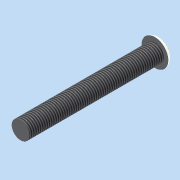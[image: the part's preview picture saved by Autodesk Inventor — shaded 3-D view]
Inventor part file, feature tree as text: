
AUTODESK INVENTOR PART (.ipt)
format: ipt  version: 2015 (Build 190159000, 159)  size: 96,256 bytes
history: native  units: mm
features: revolve x1, fillet x1, thread x1, sketch x1
ambient origin geometry x8: Origin, YZ Plane, XZ Plane, XY Plane, X Axis, Y Axis, Z Axis, Center Point
bodies: Solid1 (feature_tree)
feature tree (4):
  revolve  "Revolution1"  [1 undecoded]
  fillet  "Fillet1"  Radius=1.0mm
  thread  "Thread1"  [1 undecoded]
  sketch  "Sketch1"  dims[d0=2.0mm d1=3.0mm d2=1.0mm d3=90.0deg d4=1.0mm d5=10.0mm d6=0.0mm d7=30.0mm]
note: 2 required parameter values undecoded (feature->parameter linkage not recoverable at this tier; creation-order binding heuristic only, values carry confidence <= 0.55)